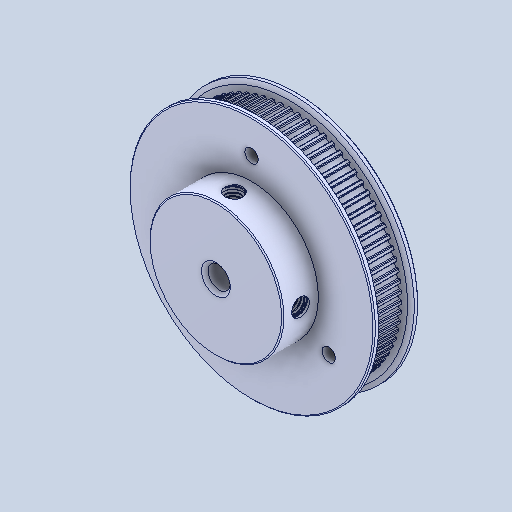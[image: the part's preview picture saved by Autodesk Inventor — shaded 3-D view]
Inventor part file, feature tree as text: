
AUTODESK INVENTOR PART (.ipt)
format: ipt  version: 2024 (Build 280153000, 153)  size: 1,915,904 bytes
history: native  units: in
note: dims shown in document units (in); Inventor stores cm internally (conversion verified against a paired STEP export)
features: other x1, extrude x1, chamfer x1
ambient origin geometry x8: Origin, YZ Plane, XZ Plane, XY Plane, X Axis, Y Axis, Z Axis, Center Point
bodies: Solid1 (feature_tree)
feature tree (3):
  other  "GT2_80T_5mm_Bore_Pulley.STEP"
  extrude  "Extrusion1"  TaperAngle=60.0deg  [1 undecoded]
  chamfer  "Chamfer3"  Angle=60.0deg  [1 undecoded]
note: 2 required parameter values undecoded (feature->parameter linkage not recoverable at this tier; creation-order binding heuristic only, values carry confidence <= 0.55)
